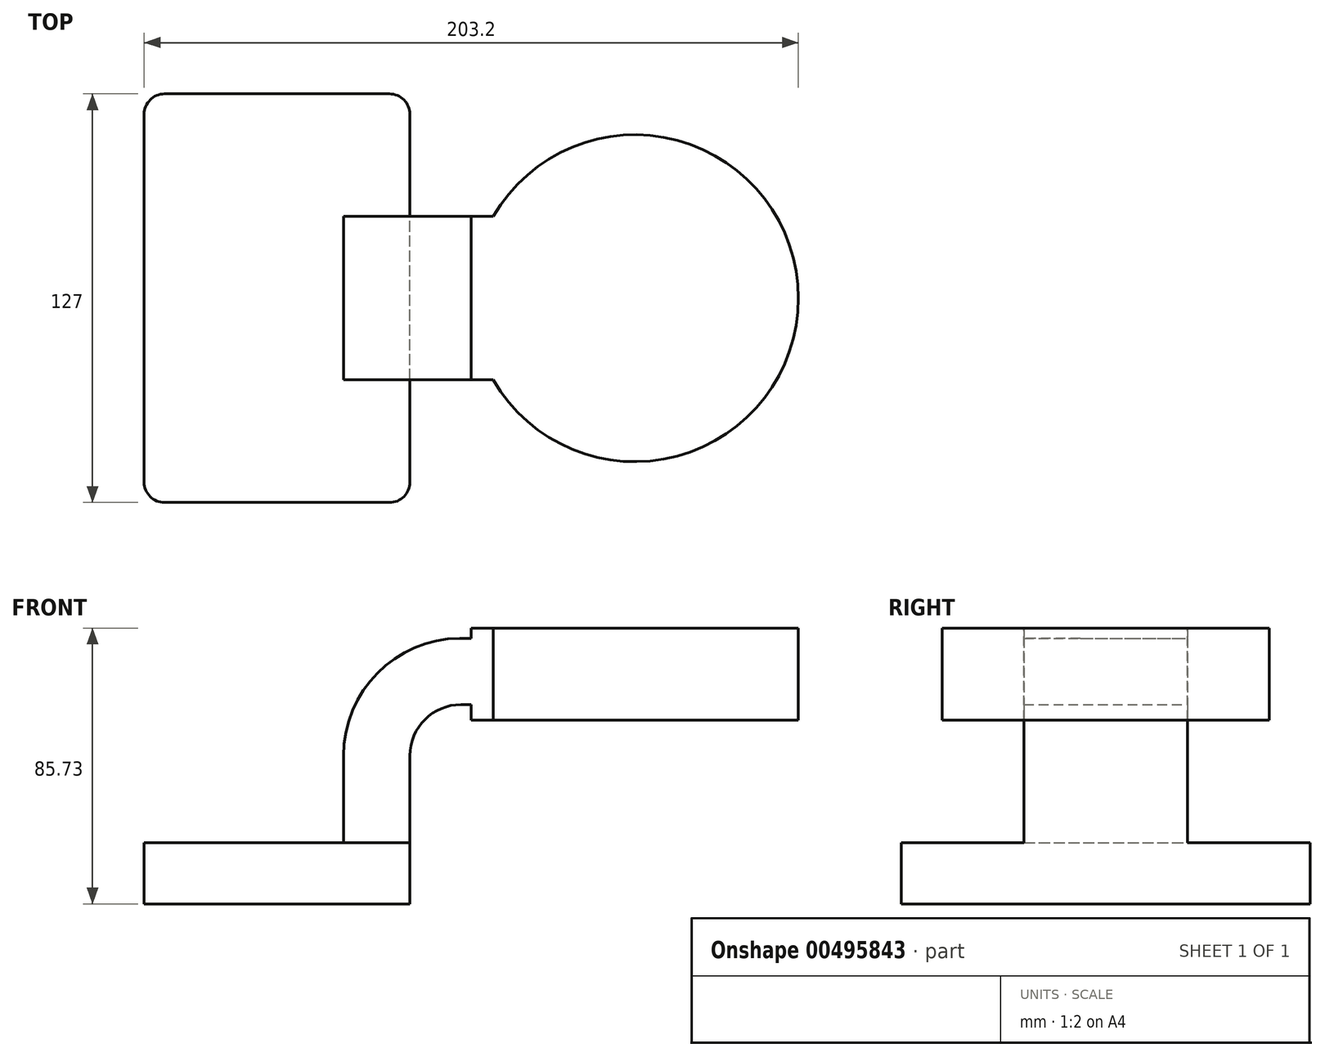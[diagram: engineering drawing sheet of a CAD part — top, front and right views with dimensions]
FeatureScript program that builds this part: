
annotation { "Feature Type Name" : "Feature", "Feature Type Description" : "" }
export const myFeature = defineFeature(function(context is Context, id is Id, definition is map)
    precondition{}
    {
        {
            var Q0;
            Q0=qCreatedBy(makeId("Front.planeOp"),FACE);
            var sketch = newSketch(context, id + "F0", { "sketchPlane" : qUnion([Q0])});
            skLineSegment(sketch, "E0.bottom", {"start": v(41.27, 9.53) * mm, "end": v(-41.28, 9.53) * mm});
            skLineSegment(sketch, "E0.top", {"start": v(41.28, -9.52) * mm, "end": v(-41.27, -9.52) * mm});
            skLineSegment(sketch, "E0.left", {"start": v(41.28, 9.53) * mm, "end": v(41.28, -9.52) * mm});
            skLineSegment(sketch, "E0.right", {"start": v(-41.28, 9.53) * mm, "end": v(-41.27, -9.52) * mm});
            skPoint(sketch, "E0.middle", {"position": v(0, 0) * mm});
            skLineSegment(sketch, "E1.bottom", {"start": v(111.12, 76.2) * mm, "end": v(60.33, 76.2) * mm});
            skLineSegment(sketch, "E1.top", {"start": v(111.12, 47.62) * mm, "end": v(60.33, 47.62) * mm});
            skLineSegment(sketch, "E1.left", {"start": v(111.12, 76.2) * mm, "end": v(111.12, 47.62) * mm});
            skLineSegment(sketch, "E1.right", {"start": v(60.32, 76.2) * mm, "end": v(60.32, 47.62) * mm});
            skPoint(sketch, "E1.middle", {"position": v(85.72, 61.91) * mm});
            skLineSegment(sketch, "E2", {"start": v(41.27, 9.53) * mm, "end": v(41.27, 36.53) * mm});
            skArc(sketch, "E3", {"start": v(41.27, 36.53) * mm, "mid": v(45.92, 47.75) * mm, "end": v(57.15, 52.4) * mm});
            skLineSegment(sketch, "E4", {"start": v(57.15, 52.4) * mm, "end": v(85.73, 52.4) * mm});
            skLineSegment(sketch, "E5.0", {"start": v(57.15, 73.01) * mm, "end": v(85.73, 73.01) * mm});
            skArc(sketch, "E5.1", {"start": v(20.66, 36.53) * mm, "mid": v(31.35, 62.33) * mm, "end": v(57.15, 73.01) * mm});
            skLineSegment(sketch, "E5.2", {"start": v(20.66, 9.53) * mm, "end": v(20.66, 36.53) * mm});
            skFitSpline(sketch, "E6", {"points": [v(-41.28, 9.52) * mm, v(57.15, 73.01) * mm], "startDerivative": vector(-0.78, 142.7) * mm, "endDerivative": vector(125.81, 0.48) * mm});
            skSolve(sketch);
        }
        {
            var Q0;
            Q0=makeQuery(id+"F0.imprint","IMPRINT",FACE,{"disambiguationData":[TD([[makeQuery(id+"F0.imprint","IMPRINT",EDGE,{"derivedFrom":sQuery(id+"F0.wireOp",EDGE,"E0.top")}),-1.0]])]});
            extrude(context, id + "F1", {"entities" : qUnion([Q0]), "endBound" : BoundingType.SYMMETRIC, "depth" : 127 * mm});
        }
        {
            var Q0;
            {var subQ1=sQuery(id+"F0.wireOp",EDGE,"E2");Q0=makeQuery(id+"F0.imprint","IMPRINT",FACE,{"disambiguationData":[TD([[makeQuery(id+"F0.imprint","IMPRINT",EDGE,{"derivedFrom":subQ1}),1.0]])]});}
            var Q1;
            {var subQ1=sQuery(id+"F0.wireOp",EDGE,"E1.bottom");Q1=makeQuery(id+"F0.imprint","IMPRINT",FACE,{"disambiguationData":[TD([[makeQuery(id+"F0.imprint","IMPRINT",EDGE,{"derivedFrom":subQ1}),1.0]])]});}
            extrude(context, id + "F2", {"entities" : qUnion([Q0, Q1]), "operationType" : NewBodyOperationType.ADD, "endBound" : BoundingType.SYMMETRIC, "depth" : 50.8 * mm});
        }
        {
            var Q0;
            {var subQ4=sQuery(id+"F0.wireOp",EDGE,"E5.1");Q0=makeQuery(id+"F0.imprint","IMPRINT",FACE,{"disambiguationData":[TD([[makeQuery(id+"F0.imprint","IMPRINT",EDGE,{"derivedFrom":subQ4}),1.0]])]});}
            extrude(context, id + "F3", {"entities" : qUnion([Q0]), "operationType" : NewBodyOperationType.ADD, "endBound" : BoundingType.SYMMETRIC, "depth" : 15.88 * mm});
        }
        {
            var Q0;
            {var subQ1=sQuery(id+"F0.wireOp",EDGE,"E1.bottom");Q0=makeQuery(id+"F0.imprint","IMPRINT",FACE,{"disambiguationData":[TD([[makeQuery(id+"F0.imprint","IMPRINT",EDGE,{"derivedFrom":subQ1}),1.0]])]});}
            var Q1;
            Q1=sQuery(id+"F0.wireOp",EDGE,"E1.left");
            revolve(context, id + "F4", {"operationType" : NewBodyOperationType.ADD, "entities" : qUnion([Q0]), "axis" : qUnion([Q1]), "revolveType" : RevolveType.FULL});
        }
        {
            var Q0;
            Q0=makeQuery(id+"F1.opExtrude","CAP_EDGE",EDGE,{"disambiguationData":[OSD([sQuery(id+"F0.wireOp",EDGE,"E0.left")])],"isStart":false});
            var Q1;
            Q1=makeQuery(id+"F1.opExtrude","CAP_EDGE",EDGE,{"disambiguationData":[OSD([sQuery(id+"F0.wireOp",EDGE,"E0.right")])],"isStart":false});
            var Q2;
            Q2=makeQuery(id+"F1.opExtrude","CAP_EDGE",EDGE,{"disambiguationData":[OSD([sQuery(id+"F0.wireOp",EDGE,"E0.left")])],"isStart":true});
            var Q3;
            Q3=makeQuery(id+"F1.opExtrude","CAP_EDGE",EDGE,{"disambiguationData":[OSD([sQuery(id+"F0.wireOp",EDGE,"E0.right")])],"isStart":true});
            fillet(context, id + "F5", {"entities" : qUnion([Q0, Q1, Q2, Q3]), "radius" : 6.35 * mm, "tangentPropagation" : true, "allowEdgeOverflow" : false});
        }
    });
